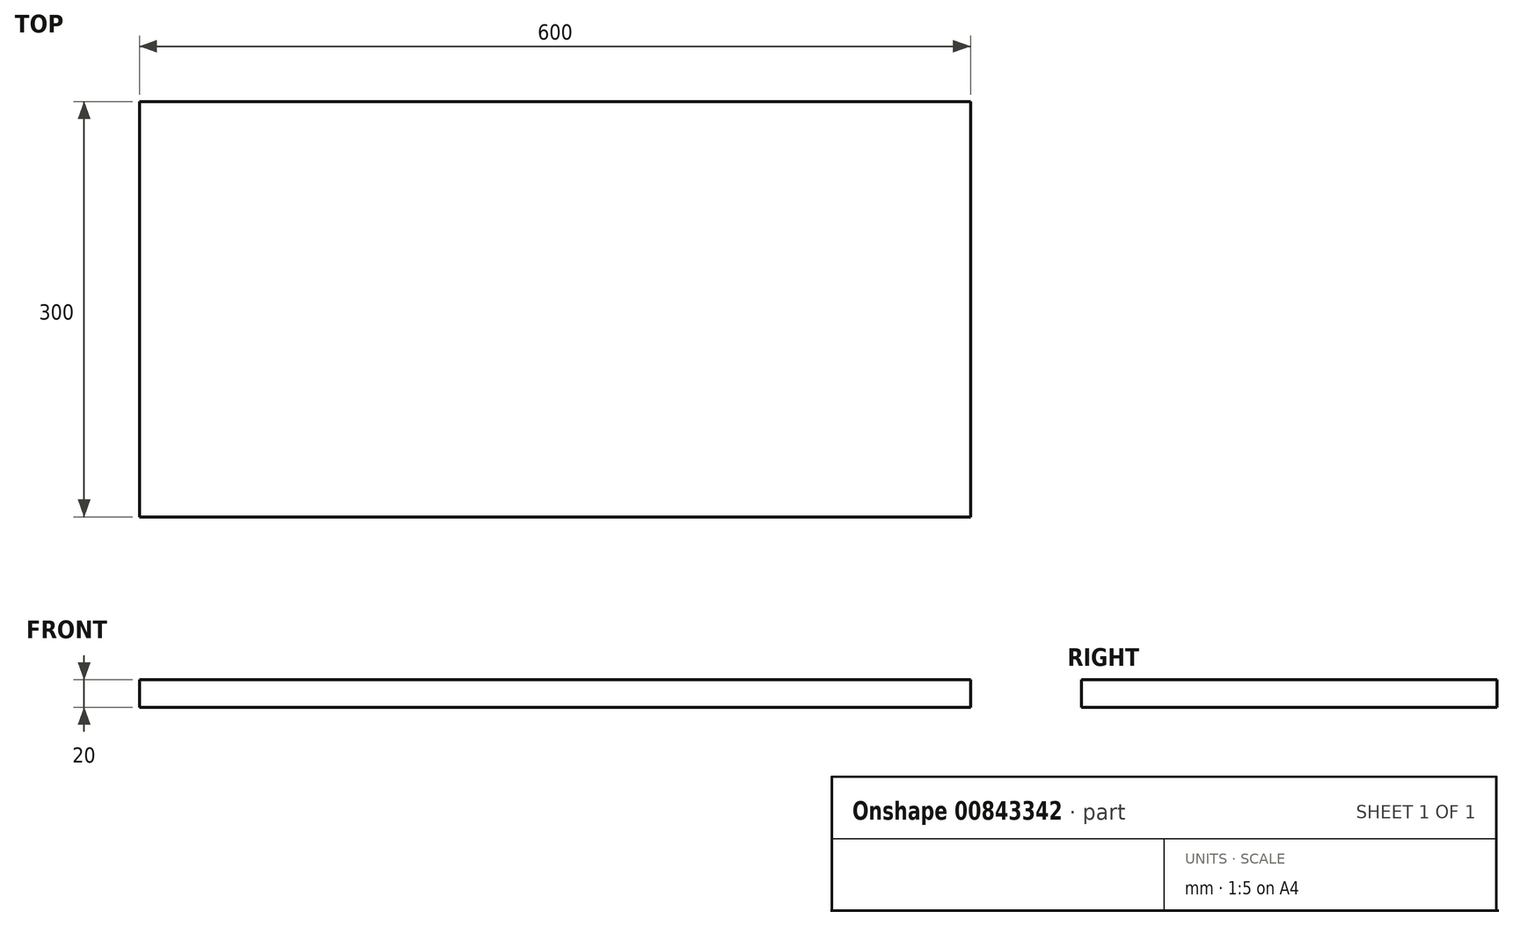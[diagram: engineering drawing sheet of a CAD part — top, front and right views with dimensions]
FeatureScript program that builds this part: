
annotation { "Feature Type Name" : "Feature", "Feature Type Description" : "" }
export const myFeature = defineFeature(function(context is Context, id is Id, definition is map)
    precondition{}
    {
        {
            var Q0;
            Q0=qCreatedBy(makeId("Top.planeOp"),FACE);
            var sketch = newSketch(context, id + "F0", { "sketchPlane" : qUnion([Q0])});
            skLineSegment(sketch, "E0.bottom", {"start": v(300, 150) * mm, "end": v(-300, 150) * mm});
            skLineSegment(sketch, "E0.top", {"start": v(300, -150) * mm, "end": v(-300, -150) * mm});
            skLineSegment(sketch, "E0.left", {"start": v(300, 150) * mm, "end": v(300, -150) * mm});
            skLineSegment(sketch, "E0.right", {"start": v(-300, 150) * mm, "end": v(-300, -150) * mm});
            skPoint(sketch, "E0.middle", {"position": v(0, 0) * mm});
            skSolve(sketch);
        }
        {
            var Q0;
            Q0 = qSketchRegion(id + "F0", true);
            extrude(context, id + "F1", {"entities" : qUnion([Q0]), "depth" : 20 * mm, "offsetDistance" : 25 * mm});
        }
    });
